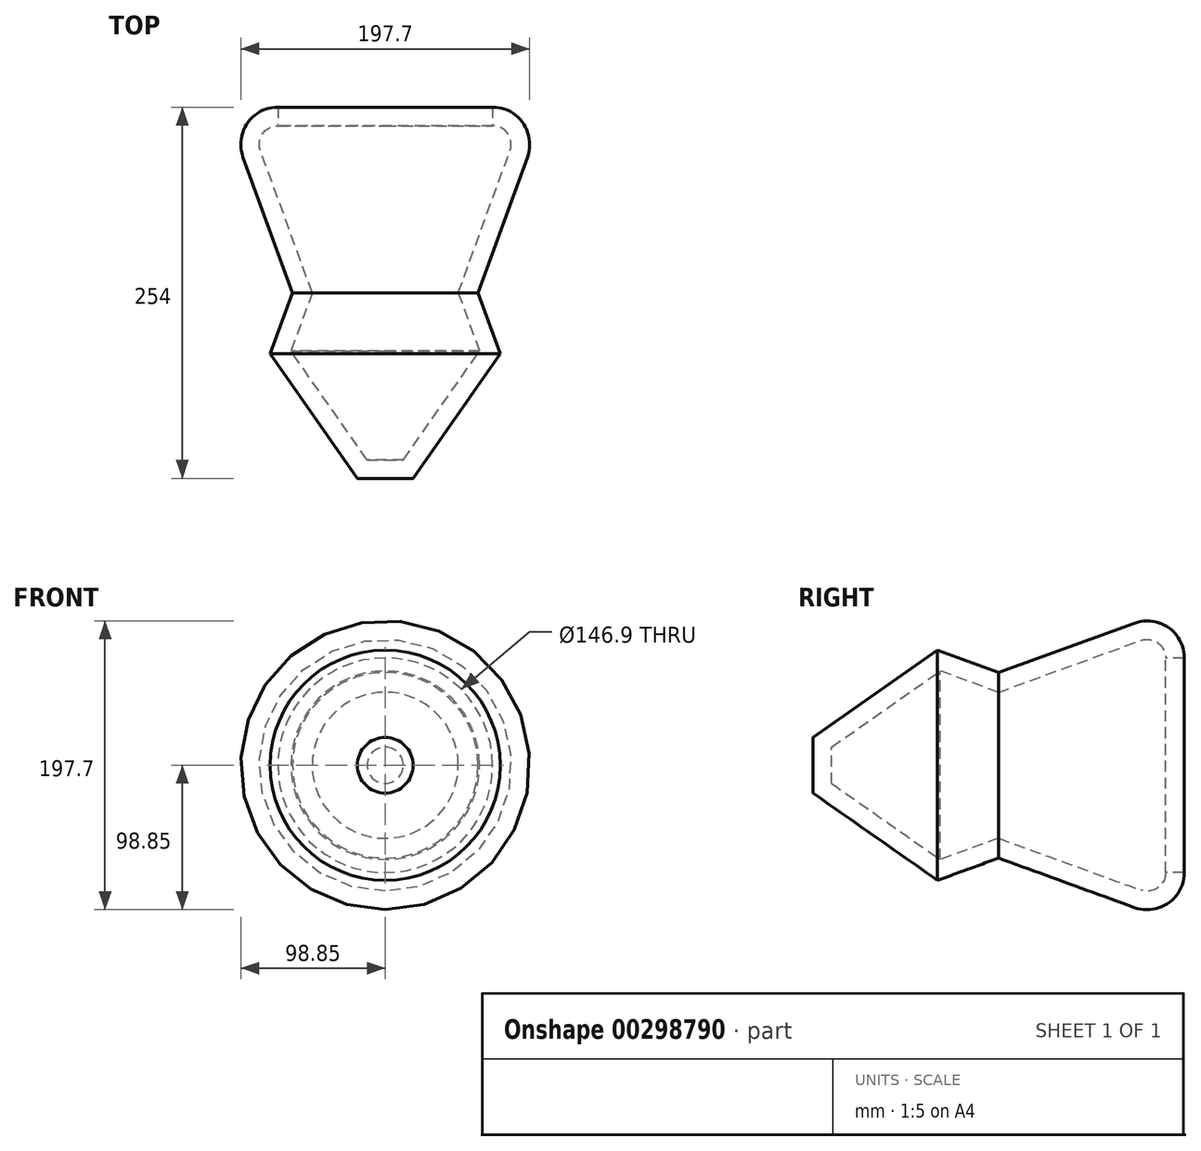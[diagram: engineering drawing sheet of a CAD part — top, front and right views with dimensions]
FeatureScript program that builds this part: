
annotation { "Feature Type Name" : "Feature", "Feature Type Description" : "" }
export const myFeature = defineFeature(function(context is Context, id is Id, definition is map)
    precondition{}
    {
        {
            var Q0;
            Q0=qCreatedBy(makeId("Front.planeOp"),FACE);
            var sketch = newSketch(context, id + "F0", { "sketchPlane" : qUnion([Q0])});
            skCircle(sketch, "E0", {"center": v(0, 0) * mm, "radius": 63.5 * mm});
            skSolve(sketch);
        }
        {
            var Q0;
            Q0=makeQuery(id+"F0.imprint","IMPRINT",FACE,{"disambiguationData":[TD([[makeQuery(id+"F0.imprint","IMPRINT",EDGE,{"derivedFrom":sQuery(id+"F0.wireOp",EDGE,"E0")}),1.0]])]});
            extrude(context, id + "F1", {"entities" : qUnion([Q0]), "endBound" : BoundingType.SYMMETRIC, "depth" : 254 * mm, "hasDraft" : true, "draftAngle" : 20 * degree});
        }
        {
            var Q0;
            Q0=makeQuery(id+"F1.opExtrude","CAP_EDGE",EDGE,{"disambiguationData":[OSD([sQuery(id+"F0.wireOp",EDGE,"E0")])],"isStart":false});
            chamfer(context, id + "F2", {"entities" : qUnion([Q0]), "width" : 63.5 * mm, "tangentPropagation" : true});
        }
        {
            var Q0;
            Q0=makeQuery(id+"F1.opExtrude","CAP_EDGE",EDGE,{"disambiguationData":[OSD([sQuery(id+"F0.wireOp",EDGE,"E0")])],"isStart":true});
            fillet(context, id + "F3", {"entities" : qUnion([Q0]), "radius" : 25.4 * mm, "tangentPropagation" : true, "allowEdgeOverflow" : false});
        }
        {
            var Q0;
            Q0=makeQuery(id+"F1.opExtrude","CAP_FACE",FACE,{"disambiguationData":[OSD([sQuery(id+"F0.wireOp",EDGE,"E0")])],"isStart":true});
            shell(context, id + "F4", {"entities" : qUnion([Q0]), "thickness" : 12.7 * mm});
        }
    });
